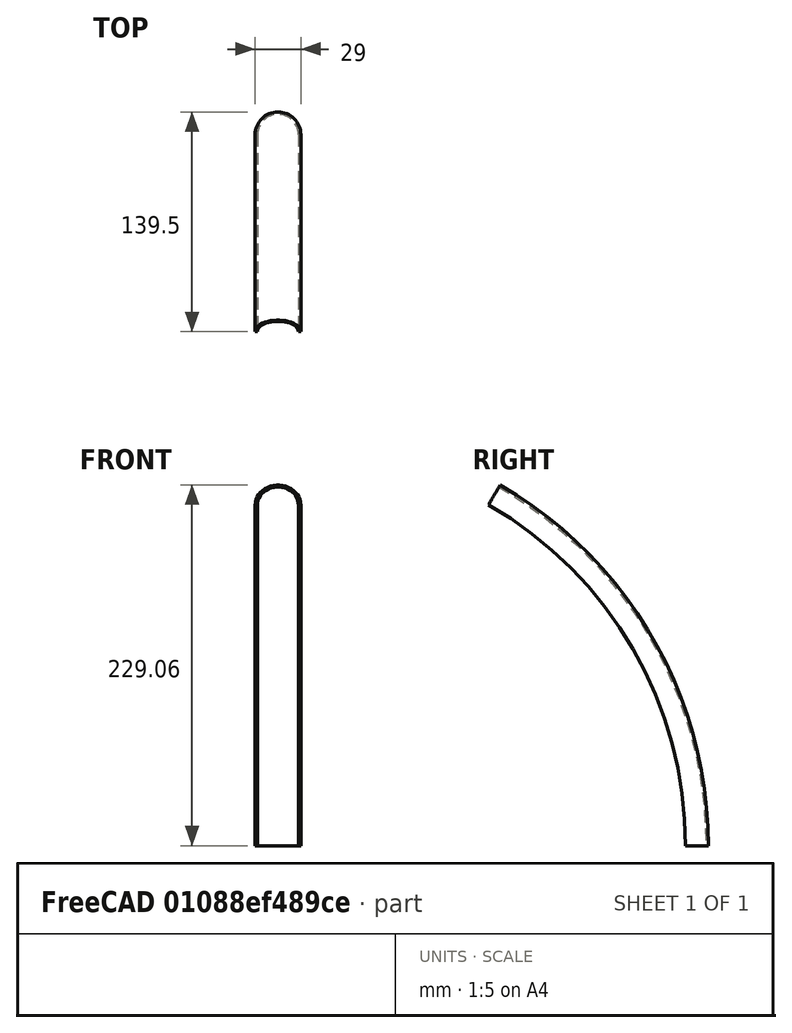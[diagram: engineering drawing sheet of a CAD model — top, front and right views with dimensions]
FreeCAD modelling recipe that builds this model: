
FCSTD DOCUMENT  (FreeCAD 0.16R)
Label: mudguard_test
License: All rights reserved
LicenseURL: http://en.wikipedia.org/wiki/All_rights_reserved
objects: Sketcher::SketchObject×2, PartDesign::Revolution×1
note: 4 computed .brp shape members not serialized (recipe doc carries the construction recipe); baked Part::Feature solids carry a one-line shape summary decoded from their .brp

FEATURE [Sketcher::SketchObject] Sketch
  sketch-geometry (4):
    g0: ArcOfCircle CenterX=0 CenterY=250 CenterZ=0 NormalX=0 NormalY=0 NormalZ=1 Radius=13 StartAngle=0 EndAngle=3.14159
    g1: ArcOfCircle CenterX=0 CenterY=250 CenterZ=0 NormalX=0 NormalY=0 NormalZ=1 Radius=14.5 StartAngle=0 EndAngle=3.14159
    g2: LineSegment StartX=14.5 StartY=250 StartZ=0 EndX=13 EndY=250 EndZ=0
    g3: LineSegment StartX=-13 StartY=250 StartZ=0 EndX=-14.5 EndY=250 EndZ=0
  constraints (14):
    c: DistanceY(g-1,g0) = 250
    c: DistanceY(g-1,g0) = 250
    c: DistanceY(g-1,g0) = 250
    c: Radius(g0) = 13
    c: DistanceX(g-1,g0) = 0
    c: Coincident(g1,g0)
    c: Radius(g1) = 14.5
    c: DistanceY(g1,g0) = 0
    c: DistanceY(g0,g1) = 0
    c: Horizontal(g3)
    c: Coincident(g3,g0)
    c: Coincident(g3,g1)
    c: Coincident(g2,g0)
    c: Coincident(g2,g1)
FEATURE [PartDesign::Revolution] Revolution
  Angle = 60
  Axis = (1,0,0)
  Base = (0,0,0)
  ReferenceAxis = -> Sketch [H_Axis]
  Sketch = -> Sketch
FEATURE [Sketcher::SketchObject] Sketch001
  Placement = pos=(0,0,0) rot=(0.57735,0.57735,0.57735;2.0944rad)
  sketch-geometry (1):
    g0: Circle CenterX=210 CenterY=-25 CenterZ=0 NormalX=0 NormalY=0 NormalZ=1 Radius=60
  constraints (3):
    c: DistanceY(g0,g-1) = 25
    c: DistanceX(g-1,g0) = 210
    c: Radius(g0) = 60
